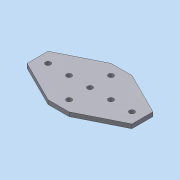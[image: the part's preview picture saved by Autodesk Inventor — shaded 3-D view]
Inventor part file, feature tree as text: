
AUTODESK INVENTOR PART (.ipt)
format: ipt  version: 2013 (Build 170138000, 138)  size: 102,400 bytes
history: native  units: mm
features: sketch x2, extrude x1, hole x1
ambient origin geometry x8: Origin, YZ Plane, XZ Plane, XY Plane, X Axis, Y Axis, Z Axis, Center Point
bodies: Solid1 (feature_tree)
feature tree (4):
  extrude  "Extrusion1"  Depth=100.0mm
  hole  "Hole1"  [1 undecoded]
  sketch  "Sketch1"  dims[d0=20.0mm d2=100.0mm]
  sketch  "Sketch2"  dims[d3=20.0mm d4=60.0mm d5=4.0mm d6=0.0mm d7=20.0mm d9=20.0mm d10=20.0mm d11=20.0mm d12=20.0mm d13=20.0mm d14=5.0mm d15=6.0mm d16=4.0mm d17=2.0mm d18=90.0deg d19=8.0mm d20=20.594885mm]
note: 1 required parameter value undecoded (feature->parameter linkage not recoverable at this tier; creation-order binding heuristic only, values carry confidence <= 0.55)
